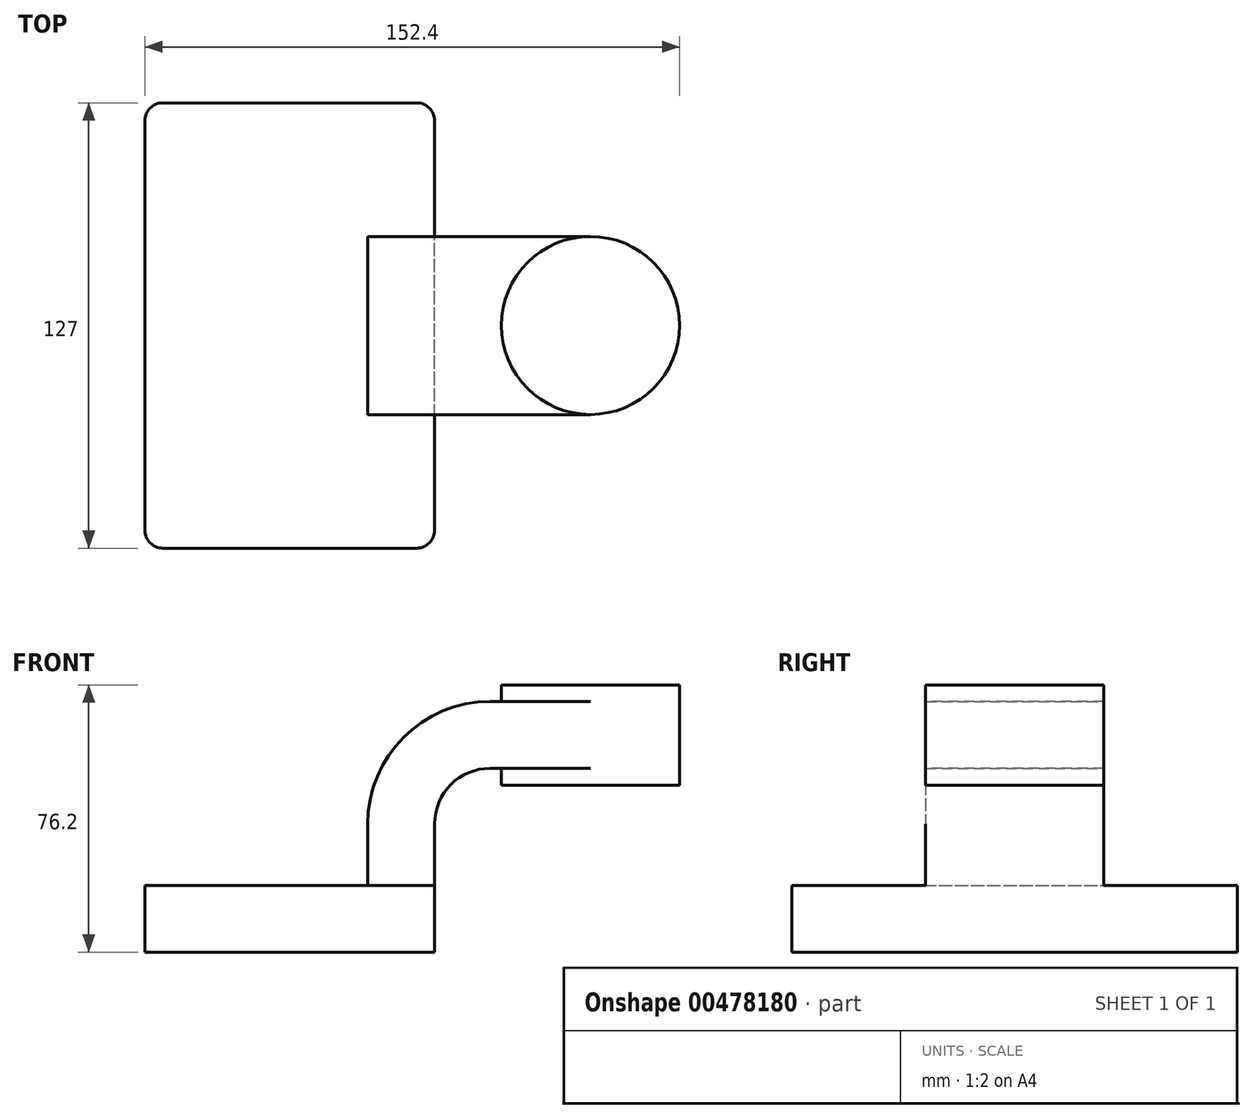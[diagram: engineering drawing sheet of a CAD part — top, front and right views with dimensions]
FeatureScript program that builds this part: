
annotation { "Feature Type Name" : "Feature", "Feature Type Description" : "" }
export const myFeature = defineFeature(function(context is Context, id is Id, definition is map)
    precondition{}
    {
        {
            var Q0;
            Q0=qCreatedBy(makeId("Front.planeOp"),FACE);
            var sketch = newSketch(context, id + "F0", { "sketchPlane" : qUnion([Q0])});
            skLineSegment(sketch, "E0.bottom", {"start": v(-14.06, 19.05) * mm, "end": v(68.49, 19.05) * mm});
            skLineSegment(sketch, "E0.top", {"start": v(-14.06, 0) * mm, "end": v(68.49, 0) * mm});
            skLineSegment(sketch, "E0.left", {"start": v(-14.06, 19.05) * mm, "end": v(-14.06, 0) * mm});
            skLineSegment(sketch, "E0.right", {"start": v(68.49, 19.05) * mm, "end": v(68.49, 0) * mm});
            skLineSegment(sketch, "E1.bottom", {"start": v(87.54, 76.2) * mm, "end": v(138.34, 76.2) * mm});
            skLineSegment(sketch, "E1.top", {"start": v(87.54, 47.62) * mm, "end": v(138.34, 47.62) * mm});
            skLineSegment(sketch, "E1.left", {"start": v(87.54, 76.2) * mm, "end": v(87.54, 47.62) * mm});
            skLineSegment(sketch, "E1.right", {"start": v(138.34, 76.2) * mm, "end": v(138.34, 47.62) * mm});
            skPoint(sketch, "E1.middle", {"position": v(112.94, 61.91) * mm});
            skLineSegment(sketch, "E2", {"start": v(68.49, 19.05) * mm, "end": v(68.49, 36.54) * mm});
            skArc(sketch, "E3", {"start": v(68.49, 36.54) * mm, "mid": v(73.14, 47.76) * mm, "end": v(84.36, 52.41) * mm});
            skLineSegment(sketch, "E4", {"start": v(84.36, 52.41) * mm, "end": v(112.94, 52.41) * mm});
            skLineSegment(sketch, "E5.0", {"start": v(84.36, 71.46) * mm, "end": v(112.94, 71.46) * mm});
            skArc(sketch, "E5.1", {"start": v(49.44, 36.54) * mm, "mid": v(59.67, 61.23) * mm, "end": v(84.36, 71.46) * mm});
            skLineSegment(sketch, "E5.2", {"start": v(49.44, 19.05) * mm, "end": v(49.44, 36.54) * mm});
            skLineSegment(sketch, "E6", {"start": v(112.94, 76.2) * mm, "end": v(112.94, 47.62) * mm});
            skFitSpline(sketch, "E7", {"points": [v(84.36, 71.46) * mm, v(-14.06, 19.05) * mm], "startDerivative": vector(-181.05, 13.28) * mm, "endDerivative": vector(-66.7, -117.47) * mm});
            skSolve(sketch);
        }
        {
            var Q0;
            Q0=makeQuery(id+"F0.imprint","IMPRINT",FACE,{"disambiguationData":[TD([[makeQuery(id+"F0.imprint","IMPRINT",EDGE,{"derivedFrom":sQuery(id+"F0.wireOp",EDGE,"E0.top")}),1.0]])]});
            extrude(context, id + "F1", {"entities" : qUnion([Q0]), "endBound" : BoundingType.SYMMETRIC, "depth" : 127 * mm});
        }
        {
            var Q0;
            {var subQ1=sQuery(id+"F0.wireOp",EDGE,"E2");Q0=makeQuery(id+"F0.imprint","IMPRINT",FACE,{"disambiguationData":[TD([[makeQuery(id+"F0.imprint","IMPRINT",EDGE,{"derivedFrom":subQ1}),1.0]])]});}
            var Q1;
            {var subQ0=sQuery(id+"F0.wireOp",EDGE,"E5.0");var subQ1=sQuery(id+"F0.wireOp",EDGE,"E1.left");var subQ2=makeQuery(id+"F0.imprint","INTERSECT",VERTEX,{"derivedFrom":[subQ1,subQ0]});Q1=makeQuery(id+"F0.imprint","IMPRINT",FACE,{"disambiguationData":[TD([[makeQuery(id+"F0.imprint","IMPRINT",EDGE,{"disambiguationData":[TD([[subQ2,-1.0]])],"derivedFrom":subQ1}),1.0]])]});}
            extrude(context, id + "F2", {"entities" : qUnion([Q0, Q1]), "operationType" : NewBodyOperationType.ADD, "endBound" : BoundingType.SYMMETRIC, "depth" : 50.8 * mm});
        }
        {
            var Q0;
            Q0=makeQuery(id+"F0.imprint","IMPRINT",FACE,{"disambiguationData":[TD([[makeQuery(id+"F0.imprint","IMPRINT",EDGE,{"derivedFrom":sQuery(id+"F0.wireOp",EDGE,"E5.1")}),1.0]])]});
            extrude(context, id + "F3", {"entities" : qUnion([Q0]), "operationType" : NewBodyOperationType.ADD, "endBound" : BoundingType.SYMMETRIC, "depth" : 12.7 * mm});
        }
        {
            var Q0;
            {var subQ0=sQuery(id+"F0.wireOp",EDGE,"E1.right");Q0=makeQuery(id+"F0.imprint","IMPRINT",FACE,{"disambiguationData":[TD([[makeQuery(id+"F0.imprint","IMPRINT",EDGE,{"derivedFrom":subQ0}),-1.0]])]});}
            var Q1;
            Q1=sQuery(id+"F0.wireOp",EDGE,"E6");
            revolve(context, id + "F4", {"operationType" : NewBodyOperationType.ADD, "entities" : qUnion([Q0]), "axis" : qUnion([Q1]), "revolveType" : RevolveType.FULL});
        }
        {
            var Q0;
            Q0=makeQuery(id+"F1.opExtrude","CAP_EDGE",EDGE,{"disambiguationData":[OSD([sQuery(id+"F0.wireOp",EDGE,"E0.left")])],"isStart":false});
            var Q1;
            Q1=makeQuery(id+"F1.opExtrude","CAP_EDGE",EDGE,{"disambiguationData":[OSD([sQuery(id+"F0.wireOp",EDGE,"E0.right")])],"isStart":false});
            var Q2;
            Q2=makeQuery(id+"F1.opExtrude","CAP_EDGE",EDGE,{"disambiguationData":[OSD([sQuery(id+"F0.wireOp",EDGE,"E0.left")])],"isStart":true});
            var Q3;
            Q3=makeQuery(id+"F1.opExtrude","CAP_EDGE",EDGE,{"disambiguationData":[OSD([sQuery(id+"F0.wireOp",EDGE,"E0.right")])],"isStart":true});
            fillet(context, id + "F5", {"entities" : qUnion([Q0, Q1, Q2, Q3]), "radius" : 5.08 * mm, "tangentPropagation" : true, "allowEdgeOverflow" : false});
        }
    });
